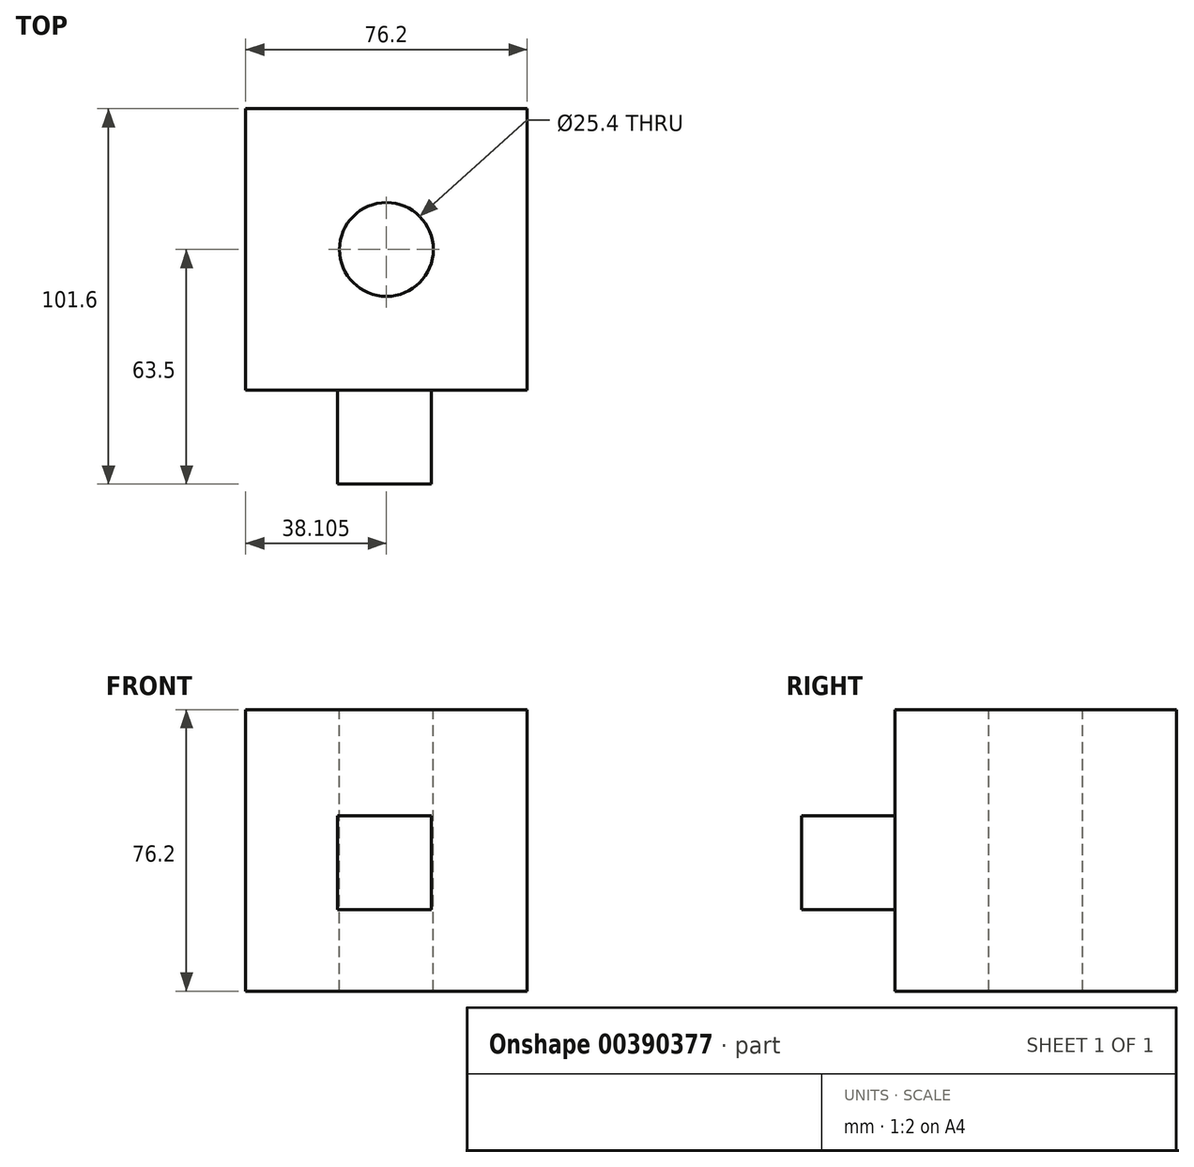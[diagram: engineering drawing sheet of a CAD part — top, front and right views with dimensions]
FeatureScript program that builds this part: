
annotation { "Feature Type Name" : "Feature", "Feature Type Description" : "" }
export const myFeature = defineFeature(function(context is Context, id is Id, definition is map)
    precondition{}
    {
        {
            var Q0;
            Q0=qCreatedBy(makeId("Front.planeOp"),FACE);
            var sketch = newSketch(context, id + "F0", { "sketchPlane" : qUnion([Q0])});
            skLineSegment(sketch, "E0.bottom", {"start": v(-34.27, 15.14) * mm, "end": v(41.93, 15.14) * mm});
            skLineSegment(sketch, "E0.top", {"start": v(-34.27, 91.34) * mm, "end": v(41.93, 91.34) * mm});
            skLineSegment(sketch, "E0.left", {"start": v(-34.27, 15.14) * mm, "end": v(-34.27, 91.34) * mm});
            skLineSegment(sketch, "E0.right", {"start": v(41.93, 15.14) * mm, "end": v(41.93, 91.34) * mm});
            skSolve(sketch);
        }
        {
            var Q0;
            Q0=makeQuery(id+"F0.imprint","IMPRINT",FACE,{"disambiguationData":[TD([[makeQuery(id+"F0.imprint","IMPRINT",EDGE,{"derivedFrom":sQuery(id+"F0.wireOp",EDGE,"E0.bottom")}),1.0]])]});
            extrude(context, id + "F1", {"entities" : qUnion([Q0]), "depth" : 76.2 * mm});
        }
        {
            var Q0;
            Q0=makeQuery(id+"F1.opExtrude","SWEPT_FACE",FACE,{"disambiguationData":[OSD([sQuery(id+"F0.wireOp",EDGE,"E0.top")])]});
            var sketch = newSketch(context, id + "F2", { "sketchPlane" : qUnion([Q0])});
            skPoint(sketch, "E1", {"position": v(3.83, -38.1) * mm});
            skSolve(sketch);
        }
        {
            var Q0;
            Q0=sQuery(id+"F2.wireOp",VERTEX,"E1");
            var Q1;
            Q1=makeQuery(id+"F1.opExtrude","SWEPT_BODY",BODY,{"disambiguationData":[OSD([sQuery(id+"F0.wireOp",EDGE,"E0.bottom"),sQuery(id+"F0.wireOp",EDGE,"E0.top"),sQuery(id+"F0.wireOp",EDGE,"E0.left"),sQuery(id+"F0.wireOp",EDGE,"E0.right")])]});
            hole(context, id + "F3", {"style" : HoleStyle.SIMPLE, "endStyle" : HoleEndStyle.THROUGH, "holeDiameter" : 25.4 * mm, "isTappedThrough" : true, "tappedDepth" : 12.7 * mm, "tapClearance" : 3, "locations" : qUnion([Q0]), "scope" : qUnion([Q1])});
        }
        {
            var Q0;
            Q0=makeQuery(id+"F1.opExtrude","CAP_FACE",FACE,{"disambiguationData":[OSD([sQuery(id+"F0.wireOp",EDGE,"E0.bottom"),sQuery(id+"F0.wireOp",EDGE,"E0.top"),sQuery(id+"F0.wireOp",EDGE,"E0.left"),sQuery(id+"F0.wireOp",EDGE,"E0.right")])],"isStart":false});
            var sketch = newSketch(context, id + "F4", { "sketchPlane" : qUnion([Q0])});
            skLineSegment(sketch, "E2.bottom", {"start": v(-9.4, 62.56) * mm, "end": v(16, 62.56) * mm});
            skLineSegment(sketch, "E2.top", {"start": v(-9.4, 37.16) * mm, "end": v(16, 37.16) * mm});
            skLineSegment(sketch, "E2.left", {"start": v(-9.4, 62.56) * mm, "end": v(-9.4, 37.16) * mm});
            skLineSegment(sketch, "E2.right", {"start": v(16, 62.56) * mm, "end": v(16, 37.16) * mm});
            skSolve(sketch);
        }
        {
            var Q0;
            Q0 = qSketchRegion(id + "F4", true);
            extrude(context, id + "F5", {"entities" : qUnion([Q0]), "operationType" : NewBodyOperationType.ADD, "depth" : 25.4 * mm});
        }
    });
